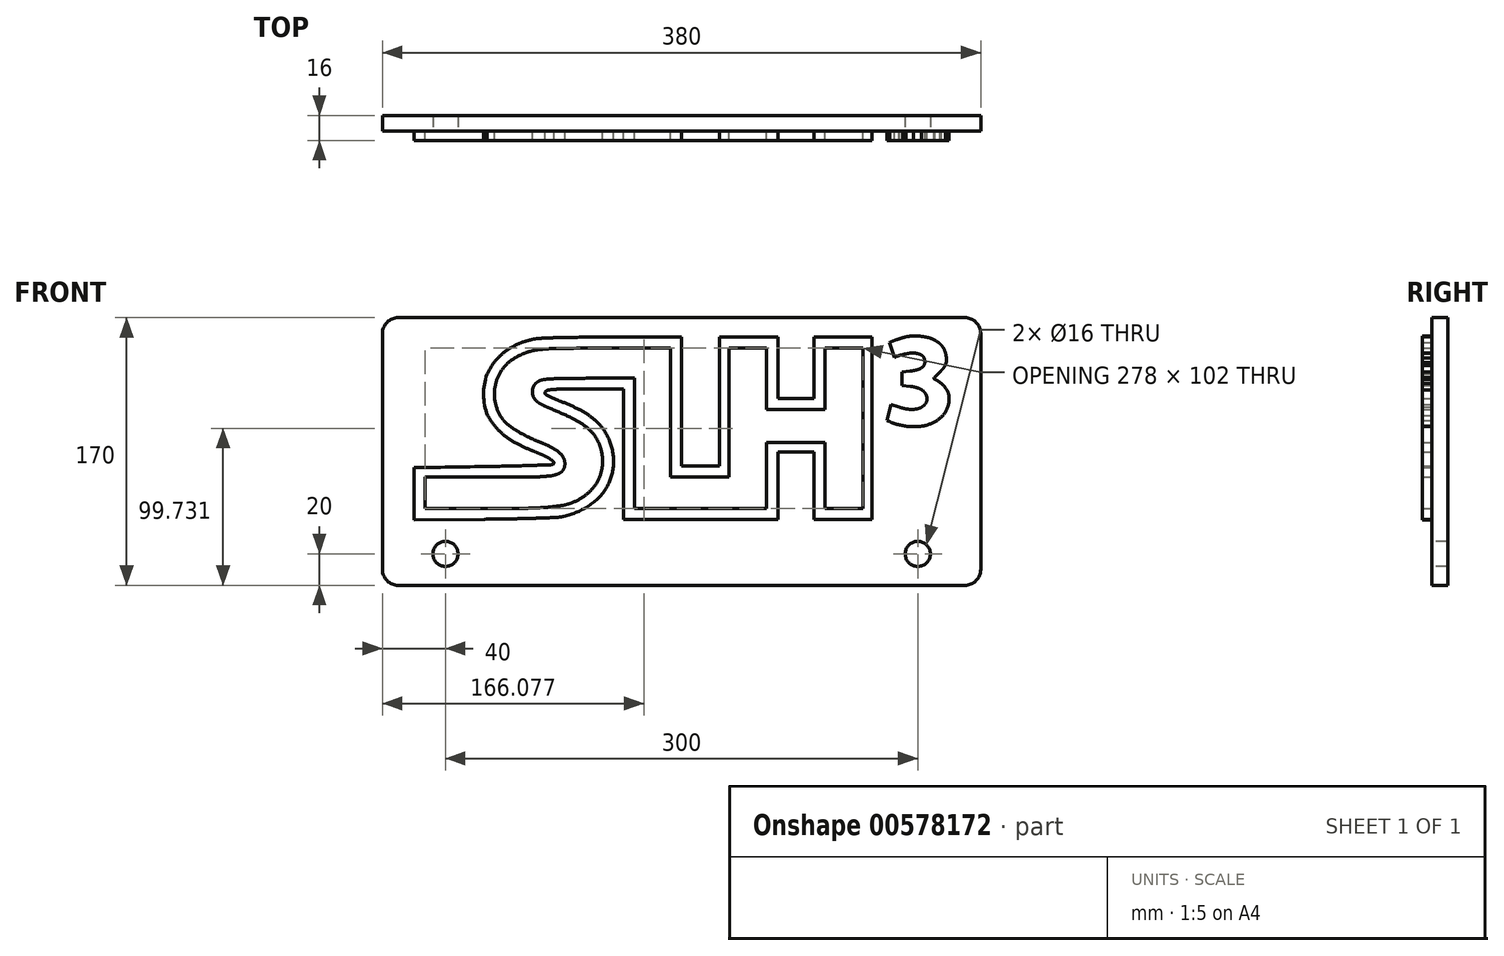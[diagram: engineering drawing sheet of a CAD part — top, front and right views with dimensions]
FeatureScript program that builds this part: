
annotation { "Feature Type Name" : "Feature", "Feature Type Description" : "" }
export const myFeature = defineFeature(function(context is Context, id is Id, definition is map)
    precondition{}
    {
        {
            var Q0;
            Q0=qCreatedBy(makeId("Front.planeOp"),FACE);
            var sketch = newSketch(context, id + "F0", { "sketchPlane" : qUnion([Q0])});
            skArc(sketch, "E0", {"start": v(147.3, 58.44) * mm, "mid": v(144.9, 58.22) * mm, "end": v(142.5, 57.82) * mm});
            skArc(sketch, "E1", {"start": v(142.5, 57.82) * mm, "mid": v(141.63, 57.59) * mm, "end": v(140.75, 57.35) * mm});
            skArc(sketch, "E2", {"start": v(140.75, 57.35) * mm, "mid": v(139.8, 57.05) * mm, "end": v(138.84, 56.75) * mm});
            skArc(sketch, "E3", {"start": v(138.84, 56.75) * mm, "mid": v(137.83, 56.42) * mm, "end": v(136.83, 56.09) * mm});
            skArc(sketch, "E4", {"start": v(136.83, 56.09) * mm, "mid": v(134.45, 55.26) * mm, "end": v(132.1, 54.33) * mm});
            skArc(sketch, "E5", {"start": v(135.3, 44.79) * mm, "mid": v(138.92, 46.14) * mm, "end": v(142.68, 47.08) * mm});
            skArc(sketch, "E6", {"start": v(142.68, 47.08) * mm, "mid": v(145.3, 47.46) * mm, "end": v(147.96, 47.48) * mm});
            skArc(sketch, "E7", {"start": v(147.96, 47.48) * mm, "mid": v(150, 47.16) * mm, "end": v(151.95, 46.48) * mm});
            skArc(sketch, "E8", {"start": v(151.95, 46.48) * mm, "mid": v(153.25, 45.54) * mm, "end": v(154.1, 44.19) * mm});
            skArc(sketch, "E9", {"start": v(154.1, 44.19) * mm, "mid": v(154.46, 42.68) * mm, "end": v(154.45, 41.13) * mm});
            skArc(sketch, "E10", {"start": v(154.45, 41.13) * mm, "mid": v(154.03, 39.82) * mm, "end": v(153.18, 38.74) * mm});
            skArc(sketch, "E11", {"start": v(153.18, 38.74) * mm, "mid": v(151.73, 37.71) * mm, "end": v(150.09, 37.04) * mm});
            skArc(sketch, "E12", {"start": v(150.09, 37.04) * mm, "mid": v(147.56, 36.44) * mm, "end": v(145, 36.04) * mm});
            skLineSegment(sketch, "E13", {"start": v(145, 36.04) * mm, "end": v(140.08, 35.45) * mm});
            skLineSegment(sketch, "E14", {"start": v(140.08, 35.45) * mm, "end": v(140.08, 31.23) * mm});
            skLineSegment(sketch, "E15", {"start": v(140.08, 31.23) * mm, "end": v(140.08, 27.01) * mm});
            skLineSegment(sketch, "E16", {"start": v(140.08, 27.01) * mm, "end": v(145.31, 26.4) * mm});
            skArc(sketch, "E17", {"start": v(145.31, 26.4) * mm, "mid": v(147.5, 26.03) * mm, "end": v(149.65, 25.5) * mm});
            skArc(sketch, "E18", {"start": v(149.65, 25.5) * mm, "mid": v(151.33, 24.84) * mm, "end": v(152.88, 23.93) * mm});
            skArc(sketch, "E19", {"start": v(152.88, 23.93) * mm, "mid": v(154.03, 22.94) * mm, "end": v(154.95, 21.74) * mm});
            skArc(sketch, "E20", {"start": v(154.95, 21.74) * mm, "mid": v(155.57, 20.42) * mm, "end": v(155.88, 19) * mm});
            skArc(sketch, "E21", {"start": v(155.88, 19) * mm, "mid": v(155.68, 16.9) * mm, "end": v(154.7, 15.06) * mm});
            skArc(sketch, "E22", {"start": v(154.7, 15.06) * mm, "mid": v(152.96, 13.47) * mm, "end": v(150.85, 12.44) * mm});
            skArc(sketch, "E23", {"start": v(150.85, 12.44) * mm, "mid": v(147.9, 11.8) * mm, "end": v(144.88, 11.77) * mm});
            skArc(sketch, "E24", {"start": v(144.88, 11.77) * mm, "mid": v(141.4, 12.3) * mm, "end": v(138.02, 13.25) * mm});
            skArc(sketch, "E25", {"start": v(130.58, 4.7) * mm, "mid": v(134.35, 3.08) * mm, "end": v(138.27, 1.86) * mm});
            skArc(sketch, "E26", {"start": v(138.27, 1.86) * mm, "mid": v(144.65, 0.87) * mm, "end": v(151.1, 0.91) * mm});
            skArc(sketch, "E27", {"start": v(151.1, 0.91) * mm, "mid": v(156.72, 2.08) * mm, "end": v(161.92, 4.5) * mm});
            skArc(sketch, "E28", {"start": v(161.92, 4.5) * mm, "mid": v(165.7, 7.66) * mm, "end": v(168.44, 11.76) * mm});
            skArc(sketch, "E29", {"start": v(168.44, 11.76) * mm, "mid": v(169.8, 16.35) * mm, "end": v(169.66, 21.14) * mm});
            skArc(sketch, "E30", {"start": v(169.66, 21.14) * mm, "mid": v(169.24, 22.6) * mm, "end": v(168.57, 23.97) * mm});
            skArc(sketch, "E31", {"start": v(168.57, 23.97) * mm, "mid": v(166.9, 26.2) * mm, "end": v(165.02, 28.24) * mm});
            skArc(sketch, "E32", {"start": v(165.02, 28.24) * mm, "mid": v(162.97, 29.65) * mm, "end": v(160.8, 30.87) * mm});
            skArc(sketch, "E33", {"start": v(160.8, 30.87) * mm, "mid": v(160.38, 31.45) * mm, "end": v(160.66, 32.1) * mm});
            skArc(sketch, "E34", {"start": v(160.66, 32.1) * mm, "mid": v(162.36, 33.8) * mm, "end": v(164.08, 35.5) * mm});
            skArc(sketch, "E35", {"start": v(164.08, 35.5) * mm, "mid": v(165.17, 36.63) * mm, "end": v(166.22, 37.8) * mm});
            skArc(sketch, "E36", {"start": v(166.22, 37.8) * mm, "mid": v(166.84, 38.64) * mm, "end": v(167.35, 39.53) * mm});
            skArc(sketch, "E37", {"start": v(167.35, 39.53) * mm, "mid": v(167.8, 40.5) * mm, "end": v(168.09, 41.53) * mm});
            skArc(sketch, "E38", {"start": v(168.09, 41.53) * mm, "mid": v(168.2, 42.88) * mm, "end": v(168.2, 44.24) * mm});
            skArc(sketch, "E39", {"start": v(168.2, 44.24) * mm, "mid": v(168, 45.88) * mm, "end": v(167.63, 47.49) * mm});
            skArc(sketch, "E40", {"start": v(167.63, 47.49) * mm, "mid": v(167.09, 49.15) * mm, "end": v(166.3, 50.72) * mm});
            skArc(sketch, "E41", {"start": v(166.3, 50.72) * mm, "mid": v(165.28, 52.17) * mm, "end": v(164.05, 53.45) * mm});
            skArc(sketch, "E42", {"start": v(164.05, 53.45) * mm, "mid": v(162.51, 54.68) * mm, "end": v(160.85, 55.74) * mm});
            skArc(sketch, "E43", {"start": v(160.85, 55.74) * mm, "mid": v(159.13, 56.56) * mm, "end": v(157.3, 57.16) * mm});
            skArc(sketch, "E44", {"start": v(157.3, 57.16) * mm, "mid": v(154.84, 57.72) * mm, "end": v(152.34, 58.13) * mm});
            skArc(sketch, "E45", {"start": v(152.34, 58.13) * mm, "mid": v(149.83, 58.36) * mm, "end": v(147.3, 58.44) * mm});
            skArc(sketch, "E46", {"start": v(-94.8, 56.19) * mm, "mid": v(-99.37, 54.96) * mm, "end": v(-103.8, 53.28) * mm});
            skArc(sketch, "E47", {"start": v(-103.8, 53.28) * mm, "mid": v(-107.86, 51.23) * mm, "end": v(-111.67, 48.76) * mm});
            skArc(sketch, "E48", {"start": v(-111.67, 48.76) * mm, "mid": v(-115.04, 45.97) * mm, "end": v(-118.08, 42.81) * mm});
            skArc(sketch, "E49", {"start": v(-118.08, 42.81) * mm, "mid": v(-121.12, 38.65) * mm, "end": v(-123.5, 34.08) * mm});
            skArc(sketch, "E50", {"start": v(-123.1, 7.94) * mm, "mid": v(-120.99, 4.39) * mm, "end": v(-118.53, 1.07) * mm});
            skArc(sketch, "E51", {"start": v(-118.53, 1.07) * mm, "mid": v(-115.75, -1.97) * mm, "end": v(-112.67, -4.7) * mm});
            skArc(sketch, "E52", {"start": v(-112.67, -4.7) * mm, "mid": v(-109, -7.38) * mm, "end": v(-105.1, -9.7) * mm});
            skArc(sketch, "E53", {"start": v(-105.1, -9.7) * mm, "mid": v(-100.3, -12.1) * mm, "end": v(-95.37, -14.24) * mm});
            skArc(sketch, "E54", {"start": v(-95.37, -14.24) * mm, "mid": v(-91.84, -15.69) * mm, "end": v(-88.34, -17.2) * mm});
            skArc(sketch, "E55", {"start": v(-88.34, -17.2) * mm, "mid": v(-86.15, -18.23) * mm, "end": v(-84.03, -19.4) * mm});
            skArc(sketch, "E56", {"start": v(-84.03, -19.4) * mm, "mid": v(-82.76, -20.23) * mm, "end": v(-81.57, -21.17) * mm});
            skArc(sketch, "E57", {"start": v(-81.57, -21.17) * mm, "mid": v(-81.17, -21.82) * mm, "end": v(-81.2, -22.58) * mm});
            skArc(sketch, "E58", {"start": v(-81.2, -22.58) * mm, "mid": v(-81.6, -23.16) * mm, "end": v(-82.27, -23.4) * mm});
            skArc(sketch, "E59", {"start": v(-82.27, -23.4) * mm, "mid": v(-89.42, -23.65) * mm, "end": v(-96.57, -23.9) * mm});
            skArc(sketch, "E60", {"start": v(-96.57, -23.9) * mm, "mid": v(-107.38, -24.2) * mm, "end": v(-118.18, -24.43) * mm});
            skArc(sketch, "E61", {"start": v(-118.18, -24.43) * mm, "mid": v(-139.68, -24.8) * mm, "end": v(-161.17, -25.13) * mm});
            skLineSegment(sketch, "E62", {"start": v(-161.17, -25.13) * mm, "end": v(-169.92, -25.27) * mm});
            skLineSegment(sketch, "E63", {"start": v(-169.92, -25.27) * mm, "end": v(-169.92, -41.9) * mm});
            skLineSegment(sketch, "E64", {"start": v(-169.92, -41.9) * mm, "end": v(-169.92, -58.54) * mm});
            skLineSegment(sketch, "E65", {"start": v(-169.92, -58.54) * mm, "end": v(-125.17, -58.01) * mm});
            skArc(sketch, "E66", {"start": v(-125.17, -58.01) * mm, "mid": v(-115.04, -57.88) * mm, "end": v(-104.91, -57.7) * mm});
            skArc(sketch, "E67", {"start": v(-104.91, -57.7) * mm, "mid": v(-97.51, -57.54) * mm, "end": v(-90.11, -57.31) * mm});
            skArc(sketch, "E68", {"start": v(-90.11, -57.31) * mm, "mid": v(-84.7, -57.1) * mm, "end": v(-79.27, -56.85) * mm});
            skArc(sketch, "E69", {"start": v(-79.27, -56.85) * mm, "mid": v(-77.08, -56.64) * mm, "end": v(-74.92, -56.25) * mm});
            skArc(sketch, "E70", {"start": v(-74.92, -56.25) * mm, "mid": v(-66.24, -53.43) * mm, "end": v(-58.23, -49.06) * mm});
            skArc(sketch, "E71", {"start": v(-58.23, -49.06) * mm, "mid": v(-51.9, -43.6) * mm, "end": v(-47.03, -36.8) * mm});
            skArc(sketch, "E72", {"start": v(-47.03, -36.8) * mm, "mid": v(-44.12, -29.35) * mm, "end": v(-43.18, -21.4) * mm});
            skArc(sketch, "E73", {"start": v(-43.18, -21.4) * mm, "mid": v(-44.2, -13.14) * mm, "end": v(-47.06, -5.32) * mm});
            skArc(sketch, "E74", {"start": v(-47.06, -5.32) * mm, "mid": v(-49.08, -1.82) * mm, "end": v(-51.5, 1.41) * mm});
            skArc(sketch, "E75", {"start": v(-51.5, 1.41) * mm, "mid": v(-54.35, 4.4) * mm, "end": v(-57.51, 7.02) * mm});
            skArc(sketch, "E76", {"start": v(-57.51, 7.02) * mm, "mid": v(-61.55, 9.74) * mm, "end": v(-65.82, 12.07) * mm});
            skArc(sketch, "E77", {"start": v(-65.82, 12.07) * mm, "mid": v(-71.57, 14.73) * mm, "end": v(-77.42, 17.15) * mm});
            skArc(sketch, "E78", {"start": v(-77.42, 17.15) * mm, "mid": v(-78.84, 17.71) * mm, "end": v(-80.25, 18.3) * mm});
            skArc(sketch, "E79", {"start": v(-80.25, 18.3) * mm, "mid": v(-81.6, 18.89) * mm, "end": v(-82.95, 19.5) * mm});
            skArc(sketch, "E80", {"start": v(-82.95, 19.5) * mm, "mid": v(-84.1, 20.05) * mm, "end": v(-85.23, 20.6) * mm});
            skArc(sketch, "E81", {"start": v(-85.23, 20.6) * mm, "mid": v(-85.84, 20.95) * mm, "end": v(-86.42, 21.34) * mm});
            skArc(sketch, "E82", {"start": v(-86.42, 21.34) * mm, "mid": v(-86.85, 22.1) * mm, "end": v(-86.6, 22.92) * mm});
            skArc(sketch, "E83", {"start": v(-86.6, 22.92) * mm, "mid": v(-85.66, 23.7) * mm, "end": v(-84.5, 24.07) * mm});
            skArc(sketch, "E84", {"start": v(-84.5, 24.07) * mm, "mid": v(-80.93, 24.44) * mm, "end": v(-77.35, 24.6) * mm});
            skArc(sketch, "E85", {"start": v(-77.35, 24.6) * mm, "mid": v(-69.26, 24.68) * mm, "end": v(-61.17, 24.72) * mm});
            skLineSegment(sketch, "E86", {"start": v(-61.17, 24.72) * mm, "end": v(-36.92, 24.73) * mm});
            skLineSegment(sketch, "E87", {"start": v(-36.92, 24.73) * mm, "end": v(-36.92, -16.77) * mm});
            skLineSegment(sketch, "E88", {"start": v(-36.92, -16.77) * mm, "end": v(-36.92, -58.27) * mm});
            skLineSegment(sketch, "E89", {"start": v(-36.92, -58.27) * mm, "end": v(12.08, -58.27) * mm});
            skLineSegment(sketch, "E90", {"start": v(12.08, -58.27) * mm, "end": v(61.08, -58.27) * mm});
            skLineSegment(sketch, "E91", {"start": v(61.08, -58.27) * mm, "end": v(61.08, -36.77) * mm});
            skLineSegment(sketch, "E92", {"start": v(61.08, -36.77) * mm, "end": v(61.08, -15.27) * mm});
            skLineSegment(sketch, "E93", {"start": v(61.08, -15.27) * mm, "end": v(72.58, -15.27) * mm});
            skLineSegment(sketch, "E94", {"start": v(72.58, -15.27) * mm, "end": v(84.08, -15.27) * mm});
            skLineSegment(sketch, "E95", {"start": v(84.08, -15.27) * mm, "end": v(84.08, -36.77) * mm});
            skLineSegment(sketch, "E96", {"start": v(84.08, -36.77) * mm, "end": v(84.08, -58.27) * mm});
            skLineSegment(sketch, "E97", {"start": v(84.08, -58.27) * mm, "end": v(102.58, -58.27) * mm});
            skLineSegment(sketch, "E98", {"start": v(102.58, -58.27) * mm, "end": v(121.08, -58.27) * mm});
            skLineSegment(sketch, "E99", {"start": v(121.08, -58.27) * mm, "end": v(121.08, -0.27) * mm});
            skLineSegment(sketch, "E100", {"start": v(121.08, -0.27) * mm, "end": v(121.08, 57.73) * mm});
            skLineSegment(sketch, "E101", {"start": v(121.08, 57.73) * mm, "end": v(102.58, 57.73) * mm});
            skLineSegment(sketch, "E102", {"start": v(102.58, 57.73) * mm, "end": v(84.08, 57.73) * mm});
            skLineSegment(sketch, "E103", {"start": v(84.08, 57.73) * mm, "end": v(84.08, 38.23) * mm});
            skLineSegment(sketch, "E104", {"start": v(84.08, 38.23) * mm, "end": v(84.08, 18.73) * mm});
            skLineSegment(sketch, "E105", {"start": v(84.08, 18.73) * mm, "end": v(72.58, 18.73) * mm});
            skLineSegment(sketch, "E106", {"start": v(72.58, 18.73) * mm, "end": v(61.08, 18.73) * mm});
            skLineSegment(sketch, "E107", {"start": v(61.08, 18.73) * mm, "end": v(61.08, 38.23) * mm});
            skLineSegment(sketch, "E108", {"start": v(61.08, 38.23) * mm, "end": v(61.08, 57.73) * mm});
            skLineSegment(sketch, "E109", {"start": v(61.08, 57.73) * mm, "end": v(42.58, 57.73) * mm});
            skLineSegment(sketch, "E110", {"start": v(42.58, 57.73) * mm, "end": v(24.08, 57.73) * mm});
            skLineSegment(sketch, "E111", {"start": v(24.08, 57.73) * mm, "end": v(24.08, 16.73) * mm});
            skLineSegment(sketch, "E112", {"start": v(24.08, 16.73) * mm, "end": v(24.08, -24.27) * mm});
            skLineSegment(sketch, "E113", {"start": v(24.08, -24.27) * mm, "end": v(12.08, -24.27) * mm});
            skLineSegment(sketch, "E114", {"start": v(12.08, -24.27) * mm, "end": v(0.08, -24.27) * mm});
            skLineSegment(sketch, "E115", {"start": v(0.08, -24.27) * mm, "end": v(0.08, 16.73) * mm});
            skLineSegment(sketch, "E116", {"start": v(0.08, 16.73) * mm, "end": v(0.08, 57.73) * mm});
            skLineSegment(sketch, "E117", {"start": v(0.08, 57.73) * mm, "end": v(-44.17, 57.65) * mm});
            skArc(sketch, "E118", {"start": v(-44.17, 57.65) * mm, "mid": v(-55.24, 57.62) * mm, "end": v(-66.31, 57.55) * mm});
            skArc(sketch, "E119", {"start": v(-66.31, 57.55) * mm, "mid": v(-73.3, 57.46) * mm, "end": v(-80.3, 57.3) * mm});
            skArc(sketch, "E120", {"start": v(-80.3, 57.3) * mm, "mid": v(-85.01, 57.12) * mm, "end": v(-89.72, 56.88) * mm});
            skArc(sketch, "E121", {"start": v(-89.72, 56.88) * mm, "mid": v(-92.27, 56.63) * mm, "end": v(-94.8, 56.19) * mm});
            skLineSegment(sketch, "E122", {"start": v(-6.92, 9.73) * mm, "end": v(-6.92, -31.27) * mm});
            skLineSegment(sketch, "E123", {"start": v(-6.92, -31.27) * mm, "end": v(11.58, -31.27) * mm});
            skLineSegment(sketch, "E124", {"start": v(11.58, -31.27) * mm, "end": v(30.08, -31.27) * mm});
            skLineSegment(sketch, "E125", {"start": v(30.08, -31.27) * mm, "end": v(30.08, 9.73) * mm});
            skLineSegment(sketch, "E126", {"start": v(30.08, 9.73) * mm, "end": v(30.08, 50.73) * mm});
            skLineSegment(sketch, "E127", {"start": v(30.08, 50.73) * mm, "end": v(42.08, 50.73) * mm});
            skLineSegment(sketch, "E128", {"start": v(42.08, 50.73) * mm, "end": v(54.08, 50.73) * mm});
            skLineSegment(sketch, "E129", {"start": v(54.08, 50.73) * mm, "end": v(54.08, 31.23) * mm});
            skLineSegment(sketch, "E130", {"start": v(54.08, 31.23) * mm, "end": v(54.08, 11.73) * mm});
            skLineSegment(sketch, "E131", {"start": v(54.08, 11.73) * mm, "end": v(72.58, 11.73) * mm});
            skLineSegment(sketch, "E132", {"start": v(72.58, 11.73) * mm, "end": v(91.08, 11.73) * mm});
            skLineSegment(sketch, "E133", {"start": v(91.08, 11.73) * mm, "end": v(91.08, 31.23) * mm});
            skLineSegment(sketch, "E134", {"start": v(91.08, 31.23) * mm, "end": v(91.08, 50.73) * mm});
            skLineSegment(sketch, "E135", {"start": v(91.08, 50.73) * mm, "end": v(103.08, 50.73) * mm});
            skLineSegment(sketch, "E136", {"start": v(103.08, 50.73) * mm, "end": v(115.08, 50.73) * mm});
            skLineSegment(sketch, "E137", {"start": v(115.08, 50.73) * mm, "end": v(115.08, -0.27) * mm});
            skLineSegment(sketch, "E138", {"start": v(115.08, -0.27) * mm, "end": v(115.08, -51.27) * mm});
            skLineSegment(sketch, "E139", {"start": v(115.08, -51.27) * mm, "end": v(103.08, -51.27) * mm});
            skLineSegment(sketch, "E140", {"start": v(103.08, -51.27) * mm, "end": v(91.08, -51.27) * mm});
            skLineSegment(sketch, "E141", {"start": v(91.08, -51.27) * mm, "end": v(91.08, -30.27) * mm});
            skLineSegment(sketch, "E142", {"start": v(91.08, -30.27) * mm, "end": v(91.08, -9.27) * mm});
            skLineSegment(sketch, "E143", {"start": v(91.08, -9.27) * mm, "end": v(72.58, -9.27) * mm});
            skLineSegment(sketch, "E144", {"start": v(72.58, -9.27) * mm, "end": v(54.08, -9.27) * mm});
            skLineSegment(sketch, "E145", {"start": v(54.08, -9.27) * mm, "end": v(54.08, -30.27) * mm});
            skLineSegment(sketch, "E146", {"start": v(54.08, -30.27) * mm, "end": v(54.08, -51.27) * mm});
            skLineSegment(sketch, "E147", {"start": v(54.08, -51.27) * mm, "end": v(12.08, -51.27) * mm});
            skLineSegment(sketch, "E148", {"start": v(12.08, -51.27) * mm, "end": v(-29.92, -51.27) * mm});
            skLineSegment(sketch, "E149", {"start": v(-29.92, -51.27) * mm, "end": v(-29.92, -9.71) * mm});
            skLineSegment(sketch, "E150", {"start": v(-29.92, -9.71) * mm, "end": v(-29.92, 31.84) * mm});
            skLineSegment(sketch, "E151", {"start": v(-29.92, 31.84) * mm, "end": v(-59.35, 31.54) * mm});
            skArc(sketch, "E152", {"start": v(-59.35, 31.54) * mm, "mid": v(-68.59, 31.43) * mm, "end": v(-77.82, 31.3) * mm});
            skArc(sketch, "E153", {"start": v(-77.82, 31.3) * mm, "mid": v(-81.4, 31.2) * mm, "end": v(-85, 30.98) * mm});
            skArc(sketch, "E154", {"start": v(-85, 30.98) * mm, "mid": v(-87, 30.75) * mm, "end": v(-88.97, 30.36) * mm});
            skArc(sketch, "E155", {"start": v(-88.97, 30.36) * mm, "mid": v(-90.35, 29.88) * mm, "end": v(-91.6, 29.13) * mm});
            skArc(sketch, "E156", {"start": v(-91.6, 29.13) * mm, "mid": v(-92.29, 28.57) * mm, "end": v(-92.92, 27.95) * mm});
            skArc(sketch, "E157", {"start": v(-92.92, 27.95) * mm, "mid": v(-93.42, 27.34) * mm, "end": v(-93.84, 26.68) * mm});
            skArc(sketch, "E158", {"start": v(-93.84, 26.68) * mm, "mid": v(-94.18, 25.95) * mm, "end": v(-94.43, 25.2) * mm});
            skArc(sketch, "E159", {"start": v(-94.43, 25.2) * mm, "mid": v(-94.62, 24.3) * mm, "end": v(-94.73, 23.39) * mm});
            skArc(sketch, "E160", {"start": v(-94.73, 23.39) * mm, "mid": v(-94.69, 21.74) * mm, "end": v(-94.29, 20.15) * mm});
            skArc(sketch, "E161", {"start": v(-94.29, 20.15) * mm, "mid": v(-93.54, 18.68) * mm, "end": v(-92.5, 17.41) * mm});
            skArc(sketch, "E162", {"start": v(-92.5, 17.41) * mm, "mid": v(-90.83, 16.03) * mm, "end": v(-88.98, 14.9) * mm});
            skArc(sketch, "E163", {"start": v(-88.98, 14.9) * mm, "mid": v(-86.09, 13.48) * mm, "end": v(-83.13, 12.2) * mm});
            skArc(sketch, "E164", {"start": v(-83.13, 12.2) * mm, "mid": v(-76.1, 9.22) * mm, "end": v(-69.2, 5.99) * mm});
            skArc(sketch, "E165", {"start": v(-69.2, 5.99) * mm, "mid": v(-64.63, 3.45) * mm, "end": v(-60.37, 0.44) * mm});
            skArc(sketch, "E166", {"start": v(-60.37, 0.44) * mm, "mid": v(-57.36, -2.33) * mm, "end": v(-54.8, -5.53) * mm});
            skArc(sketch, "E167", {"start": v(-54.8, -5.53) * mm, "mid": v(-52.8, -9.04) * mm, "end": v(-51.36, -12.83) * mm});
            skArc(sketch, "E168", {"start": v(-51.36, -12.83) * mm, "mid": v(-50.33, -18.12) * mm, "end": v(-50.26, -23.51) * mm});
            skArc(sketch, "E169", {"start": v(-50.26, -23.51) * mm, "mid": v(-51.18, -28.63) * mm, "end": v(-53.1, -33.46) * mm});
            skArc(sketch, "E170", {"start": v(-53.1, -33.46) * mm, "mid": v(-56, -37.9) * mm, "end": v(-59.7, -41.69) * mm});
            skArc(sketch, "E171", {"start": v(-59.7, -41.69) * mm, "mid": v(-64.29, -44.96) * mm, "end": v(-69.35, -47.44) * mm});
            skArc(sketch, "E172", {"start": v(-69.35, -47.44) * mm, "mid": v(-72.87, -48.6) * mm, "end": v(-76.49, -49.38) * mm});
            skArc(sketch, "E173", {"start": v(-76.49, -49.38) * mm, "mid": v(-81.5, -50.05) * mm, "end": v(-86.52, -50.5) * mm});
            skArc(sketch, "E174", {"start": v(-86.52, -50.5) * mm, "mid": v(-93.97, -50.9) * mm, "end": v(-101.43, -51.1) * mm});
            skArc(sketch, "E175", {"start": v(-101.43, -51.1) * mm, "mid": v(-113.71, -51.23) * mm, "end": v(-126, -51.27) * mm});
            skLineSegment(sketch, "E176", {"start": v(-126, -51.27) * mm, "end": v(-162.92, -51.27) * mm});
            skLineSegment(sketch, "E177", {"start": v(-162.92, -51.27) * mm, "end": v(-162.92, -41.27) * mm});
            skLineSegment(sketch, "E178", {"start": v(-162.92, -41.27) * mm, "end": v(-162.92, -31.27) * mm});
            skLineSegment(sketch, "E179", {"start": v(-162.92, -31.27) * mm, "end": v(-122.9, -31.27) * mm});
            skArc(sketch, "E180", {"start": v(-122.9, -31.27) * mm, "mid": v(-108.61, -31.24) * mm, "end": v(-94.33, -31.15) * mm});
            skArc(sketch, "E181", {"start": v(-94.33, -31.15) * mm, "mid": v(-88.88, -30.96) * mm, "end": v(-83.45, -30.5) * mm});
            skArc(sketch, "E182", {"start": v(-83.45, -30.5) * mm, "mid": v(-80.59, -29.95) * mm, "end": v(-77.85, -28.95) * mm});
            skArc(sketch, "E183", {"start": v(-77.85, -28.95) * mm, "mid": v(-76.05, -27.7) * mm, "end": v(-74.8, -25.9) * mm});
            skArc(sketch, "E184", {"start": v(-74.8, -25.9) * mm, "mid": v(-74.16, -23.65) * mm, "end": v(-74.23, -21.31) * mm});
            skArc(sketch, "E185", {"start": v(-74.23, -21.31) * mm, "mid": v(-75, -19.02) * mm, "end": v(-76.36, -17.03) * mm});
            skArc(sketch, "E186", {"start": v(-76.36, -17.03) * mm, "mid": v(-78.8, -14.77) * mm, "end": v(-81.58, -12.95) * mm});
            skArc(sketch, "E187", {"start": v(-81.58, -12.95) * mm, "mid": v(-85.86, -10.8) * mm, "end": v(-90.26, -8.91) * mm});
            skArc(sketch, "E188", {"start": v(-90.26, -8.91) * mm, "mid": v(-94.22, -7.25) * mm, "end": v(-98.12, -5.45) * mm});
            skArc(sketch, "E189", {"start": v(-98.12, -5.45) * mm, "mid": v(-101.59, -3.65) * mm, "end": v(-104.96, -1.68) * mm});
            skArc(sketch, "E190", {"start": v(-104.96, -1.68) * mm, "mid": v(-107.71, 0.13) * mm, "end": v(-110.36, 2.1) * mm});
            skArc(sketch, "E191", {"start": v(-110.36, 2.1) * mm, "mid": v(-112.17, 3.75) * mm, "end": v(-113.73, 5.62) * mm});
            skArc(sketch, "E192", {"start": v(-113.73, 5.62) * mm, "mid": v(-116.54, 10.5) * mm, "end": v(-118.28, 15.85) * mm});
            skArc(sketch, "E193", {"start": v(-118.28, 15.85) * mm, "mid": v(-118.88, 21.44) * mm, "end": v(-118.3, 27.04) * mm});
            skArc(sketch, "E194", {"start": v(-118.3, 27.04) * mm, "mid": v(-116.6, 32.37) * mm, "end": v(-113.82, 37.23) * mm});
            skArc(sketch, "E195", {"start": v(-113.82, 37.23) * mm, "mid": v(-110.1, 41.37) * mm, "end": v(-105.6, 44.63) * mm});
            skArc(sketch, "E196", {"start": v(-105.6, 44.63) * mm, "mid": v(-101.86, 46.53) * mm, "end": v(-97.96, 48.06) * mm});
            skArc(sketch, "E197", {"start": v(-97.96, 48.06) * mm, "mid": v(-94.07, 49.13) * mm, "end": v(-90.08, 49.77) * mm});
            skArc(sketch, "E198", {"start": v(-90.08, 49.77) * mm, "mid": v(-83.94, 50.27) * mm, "end": v(-77.78, 50.48) * mm});
            skArc(sketch, "E199", {"start": v(-77.78, 50.48) * mm, "mid": v(-62.98, 50.6) * mm, "end": v(-48.17, 50.67) * mm});
            skLineSegment(sketch, "E200", {"start": v(-48.17, 50.67) * mm, "end": v(-6.92, 50.73) * mm});
            skLineSegment(sketch, "E201", {"start": v(-6.92, 50.73) * mm, "end": v(-6.92, 9.73) * mm});
            skLineSegment(sketch, "E202", {"start": v(138.02, 13.25) * mm, "end": v(133.12, 14.81) * mm});
            skArc(sketch, "E203", {"start": v(-123.5, 34.08) * mm, "mid": v(-125.77, 20.97) * mm, "end": v(-123.1, 7.94) * mm});
            skLineSegment(sketch, "E204", {"start": v(133.12, 14.81) * mm, "end": v(130.58, 4.7) * mm});
            skLineSegment(sketch, "E205", {"start": v(132.1, 54.33) * mm, "end": v(135.3, 44.79) * mm});
            skSolve(sketch);
        }
        {
            var Q0;
            Q0 = qSketchRegion(id + "F0", true);
            extrude(context, id + "F1", {"entities" : qUnion([Q0]), "depth" : 6 * mm, "offsetDistance" : 25 * mm});
        }
        {
            var Q0;
            Q0=qCreatedBy(makeId("Front.planeOp"),FACE);
            var sketch = newSketch(context, id + "F2", { "sketchPlane" : qUnion([Q0])});
            skLineSegment(sketch, "E206.bottom", {"start": v(-190, 70) * mm, "end": v(190, 70) * mm});
            skLineSegment(sketch, "E206.top", {"start": v(-190, -100) * mm, "end": v(190, -100) * mm});
            skLineSegment(sketch, "E206.left", {"start": v(-190, 70) * mm, "end": v(-190, -100) * mm});
            skLineSegment(sketch, "E206.right", {"start": v(190, 70) * mm, "end": v(190, -100) * mm});
            skCircle(sketch, "E207", {"center": v(-150, -80) * mm, "radius": 8 * mm});
            skCircle(sketch, "E208", {"center": v(150, -80) * mm, "radius": 8 * mm});
            skLineSegment(sketch, "E209", {"start": v(-150, -80) * mm, "end": v(150, -80) * mm, "construction": true});
            skSolve(sketch);
        }
        {
            var Q0;
            Q0 = qSketchRegion(id + "F2", true);
            extrude(context, id + "F3", {"entities" : qUnion([Q0]), "oppositeDirection" : true, "depth" : 10 * mm, "offsetDistance" : 25 * mm});
        }
        {
            var Q0;
            Q0=makeQuery(id+"F3.opExtrude","SWEPT_EDGE",EDGE,{"disambiguationData":[OSD([sQuery(id+"F2.wireOp",EDGE,"E206.bottom"),sQuery(id+"F2.wireOp",EDGE,"E206.left")])]});
            var Q1;
            Q1=makeQuery(id+"F3.opExtrude","SWEPT_EDGE",EDGE,{"disambiguationData":[OSD([sQuery(id+"F2.wireOp",EDGE,"E206.top"),sQuery(id+"F2.wireOp",EDGE,"E206.left")])]});
            var Q2;
            Q2=makeQuery(id+"F3.opExtrude","SWEPT_EDGE",EDGE,{"disambiguationData":[OSD([sQuery(id+"F2.wireOp",EDGE,"E206.top"),sQuery(id+"F2.wireOp",EDGE,"E206.right")])]});
            var Q3;
            Q3=makeQuery(id+"F3.opExtrude","SWEPT_EDGE",EDGE,{"disambiguationData":[OSD([sQuery(id+"F2.wireOp",EDGE,"E206.bottom"),sQuery(id+"F2.wireOp",EDGE,"E206.right")])]});
            fillet(context, id + "F4", {"entities" : qUnion([Q0, Q1, Q2, Q3]), "radius" : 10 * mm, "tangentPropagation" : true, "allowEdgeOverflow" : false});
        }
    });
